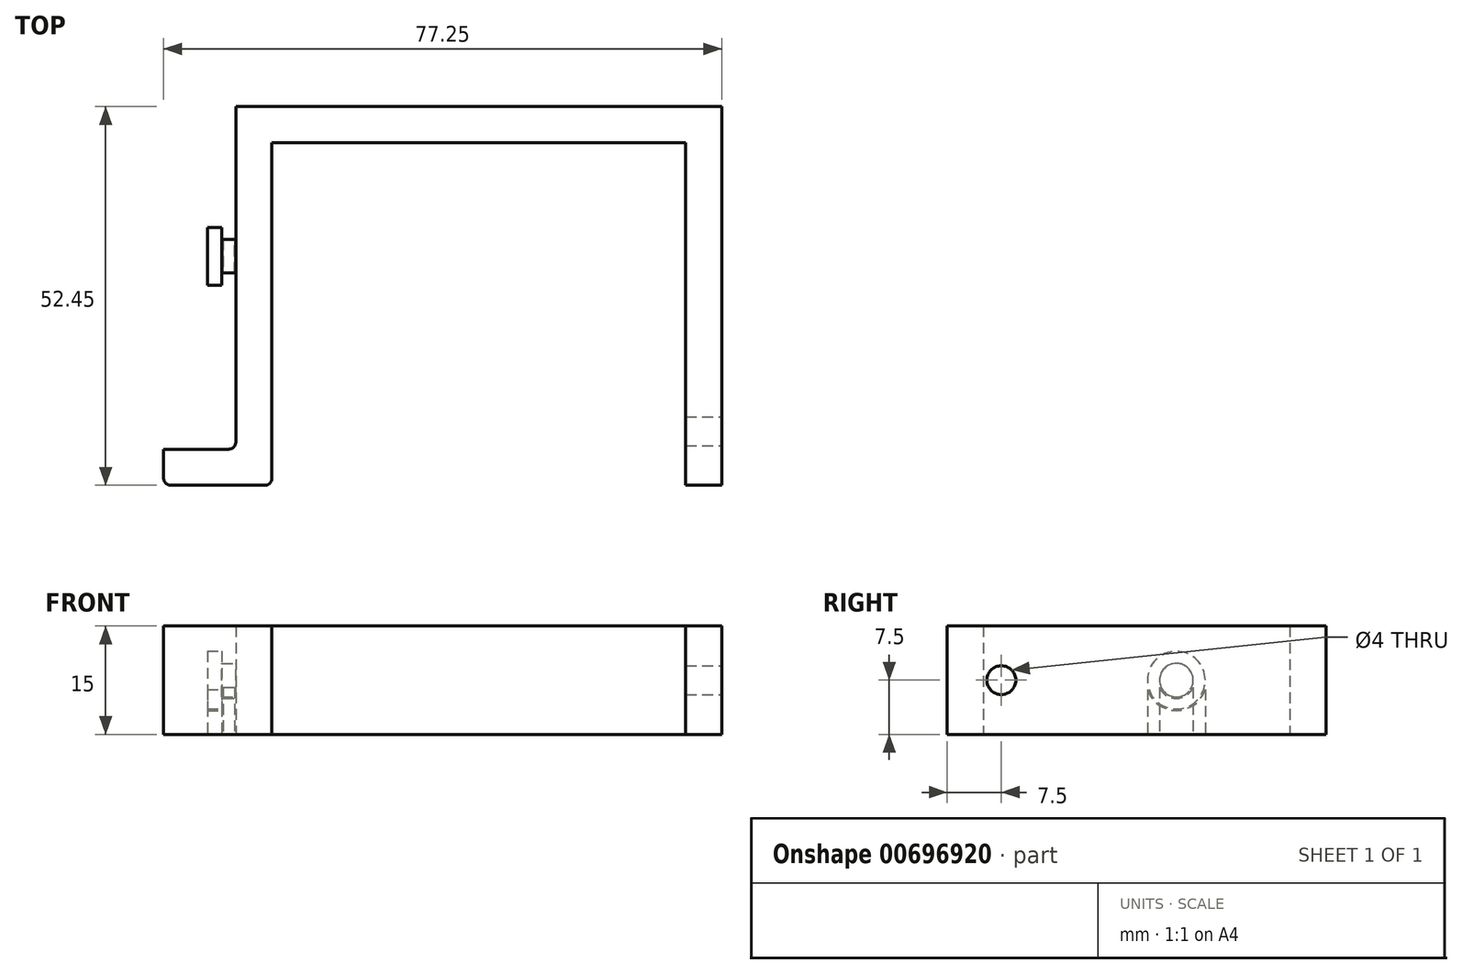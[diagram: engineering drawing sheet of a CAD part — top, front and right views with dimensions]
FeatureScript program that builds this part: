
annotation { "Feature Type Name" : "Feature", "Feature Type Description" : "" }
export const myFeature = defineFeature(function(context is Context, id is Id, definition is map)
    precondition{}
    {
        {
            var Q0;
            Q0=qCreatedBy(makeId("Top.planeOp"),FACE);
            var sketch = newSketch(context, id + "F0", { "sketchPlane" : qUnion([Q0])});
            skLineSegment(sketch, "E0.top", {"start": v(0, 20.15) * mm, "end": v(57.25, 20.15) * mm});
            skLineSegment(sketch, "E0.left", {"start": v(0, 0) * mm, "end": v(0, 20.15) * mm});
            skLineSegment(sketch, "E1.top", {"start": v(-5, 25.15) * mm, "end": v(62.25, 25.15) * mm});
            skLineSegment(sketch, "E2", {"start": v(-5, 25.15) * mm, "end": v(-5, 0) * mm});
            skLineSegment(sketch, "E3", {"start": v(0, 0) * mm, "end": v(0, -22.3) * mm});
            skLineSegment(sketch, "E4", {"start": v(-5, 0) * mm, "end": v(-5, -22.3) * mm});
            skLineSegment(sketch, "E5.bottom", {"start": v(-5, -22.3) * mm, "end": v(-15, -22.3) * mm});
            skLineSegment(sketch, "E5.top", {"start": v(0, -27.3) * mm, "end": v(-15, -27.3) * mm});
            skLineSegment(sketch, "E5.left", {"start": v(0, -22.3) * mm, "end": v(0, -27.3) * mm});
            skLineSegment(sketch, "E5.right", {"start": v(-15, -22.3) * mm, "end": v(-15, -27.3) * mm});
            skLineSegment(sketch, "E6", {"start": v(62.25, 25.15) * mm, "end": v(62.25, -27.3) * mm});
            skLineSegment(sketch, "E7", {"start": v(57.25, 20.15) * mm, "end": v(57.25, -27.3) * mm});
            skLineSegment(sketch, "E8", {"start": v(57.25, -27.3) * mm, "end": v(62.25, -27.3) * mm});
            skSolve(sketch);
        }
        {
            var Q0;
            Q0 = qSketchRegion(id + "F0", true);
            extrude(context, id + "F1", {"entities" : qUnion([Q0]), "depth" : 15 * mm, "offsetDistance" : 25 * mm});
        }
        {
            var Q0;
            Q0=makeQuery(id+"F1.opExtrude","SWEPT_FACE",FACE,{"disambiguationData":[OSD([sQuery(id+"F0.wireOp",EDGE,"E2")])]});
            var sketch = newSketch(context, id + "F2", { "sketchPlane" : qUnion([Q0])});
            skCircle(sketch, "E9", {"center": v(-4.42, 7.5) * mm, "radius": 2.33 * mm});
            skArc(sketch, "E10", {"start": v(-6.75, 6.52) * mm, "mid": v(-4.42, 4.97) * mm, "end": v(-2.1, 6.52) * mm});
            skLineSegment(sketch, "E11", {"start": v(-6.75, 6.52) * mm, "end": v(-6.75, 0) * mm});
            skLineSegment(sketch, "E12", {"start": v(-2.1, 6.52) * mm, "end": v(-2.1, 0) * mm});
            skLineSegment(sketch, "E13", {"start": v(-2.1, 0) * mm, "end": v(-6.75, 0) * mm});
            skPoint(sketch, "E14.orphan", {"position": v(-6.75, 7.5) * mm});
            skPoint(sketch, "E15.orphan", {"position": v(-2.1, 7.5) * mm});
            skSolve(sketch);
        }
        {
            var Q0;
            Q0 = qSketchRegion(id + "F2", true);
            extrude(context, id + "F3", {"entities" : qUnion([Q0]), "operationType" : NewBodyOperationType.ADD, "depth" : 1.95 * mm, "offsetDistance" : 25 * mm});
        }
        {
            var Q0;
            Q0=makeQuery(id+"F3.opExtrude","CAP_FACE",FACE,{"disambiguationData":[OSD([sQuery(id+"F2.wireOp",EDGE,"E9")])],"isStart":false});
            var sketch = newSketch(context, id + "F4", { "sketchPlane" : qUnion([Q0])});
            skCircle(sketch, "E16", {"center": v(-4.42, 7.5) * mm, "radius": 4 * mm});
            skLineSegment(sketch, "E17", {"start": v(-8.42, 6.22) * mm, "end": v(-8.42, 0) * mm});
            skLineSegment(sketch, "E18", {"start": v(-0.42, 6.22) * mm, "end": v(-0.42, 0) * mm});
            skLineSegment(sketch, "E19", {"start": v(-0.42, 0) * mm, "end": v(-8.42, 0) * mm});
            skArc(sketch, "E20", {"start": v(-8.42, 6.22) * mm, "mid": v(-4.42, 3.3) * mm, "end": v(-0.42, 6.22) * mm});
            skPoint(sketch, "E21.orphan", {"position": v(-8.42, 7.5) * mm});
            skPoint(sketch, "E22.orphan", {"position": v(-0.42, 7.5) * mm});
            skSolve(sketch);
        }
        {
            var Q0;
            Q0 = qSketchRegion(id + "F4", true);
            extrude(context, id + "F5", {"entities" : qUnion([Q0]), "operationType" : NewBodyOperationType.ADD, "depth" : 2 * mm, "offsetDistance" : 25 * mm});
        }
        {
            var Q0;
            Q0=makeQuery(id+"F5.boolean.opBoolean","MERGE",FACE,{"derivedFrom":[makeQuery(id+"F3.boolean.opBoolean","MERGE",FACE,{"derivedFrom":[makeQuery(id+"F1.opExtrude","CAP_FACE",FACE,{"disambiguationData":[OSD([sQuery(id+"F0.wireOp",EDGE,"E0.top"),sQuery(id+"F0.wireOp",EDGE,"E0.left"),sQuery(id+"F0.wireOp",EDGE,"E0.right"),sQuery(id+"F0.wireOp",EDGE,"E1.top"),sQuery(id+"F0.wireOp",EDGE,"E1.right"),sQuery(id+"F0.wireOp",EDGE,"962DIITk-y9DG-CVLt-9h3L-DnA35yfKHCaI"),sQuery(id+"F0.wireOp",EDGE,"IBw1vZgg-cOK9-ItiV-ksws-nT7VTr6wvGIP"),sQuery(id+"F0.wireOp",EDGE,"E2"),sQuery(id+"F0.wireOp",EDGE,"gIwaJglO-ZnYY-fk6S-nZtS-CVbH9vVCVLog")])],"isStart":true}),makeQuery(id+"F3.opExtrude","SWEPT_FACE",FACE,{"disambiguationData":[OSD([sQuery(id+"F2.wireOp",EDGE,"E13")])]})]}),makeQuery(id+"F5.opExtrude","SWEPT_FACE",FACE,{"disambiguationData":[OSD([sQuery(id+"F4.wireOp",EDGE,"E19")])]})]});
            var sketch = newSketch(context, id + "F6", { "sketchPlane" : qUnion([Q0])});
            skLineSegment(sketch, "E23.bottom", {"start": v(-5, -2.1) * mm, "end": v(-5.2, -2.1) * mm});
            skLineSegment(sketch, "E23.top", {"start": v(-5, -6.75) * mm, "end": v(-5.2, -6.75) * mm});
            skLineSegment(sketch, "E23.left", {"start": v(-5, -2.1) * mm, "end": v(-5, -6.75) * mm});
            skLineSegment(sketch, "E23.right", {"start": v(-5.2, -2.1) * mm, "end": v(-5.2, -6.75) * mm});
            skLineSegment(sketch, "E24.bottom", {"start": v(-6.95, -2.1) * mm, "end": v(-6.75, -2.1) * mm});
            skLineSegment(sketch, "E24.top", {"start": v(-6.95, -6.75) * mm, "end": v(-6.75, -6.75) * mm});
            skLineSegment(sketch, "E24.left", {"start": v(-6.95, -2.1) * mm, "end": v(-6.95, -6.75) * mm});
            skLineSegment(sketch, "E24.right", {"start": v(-6.75, -2.1) * mm, "end": v(-6.75, -6.75) * mm});
            skSolve(sketch);
        }
        {
            var Q0;
            Q0 = qSketchRegion(id + "F6", true);
            var Q1;
            Q1=makeQuery(id+"F3.opExtrude","SWEPT_FACE",FACE,{"disambiguationData":[OSD([sQuery(id+"F2.wireOp",EDGE,"E10")])]});
            extrude(context, id + "F7", {"entities" : qUnion([Q0]), "operationType" : NewBodyOperationType.REMOVE, "endBound" : BoundingType.UP_TO_SURFACE, "oppositeDirection" : true, "depth" : 25 * mm, "endBoundEntityFace" : qUnion([Q1]), "offsetDistance" : 25 * mm});
        }
        {
            var Q0;
            Q0=makeQuery(id+"F1.opExtrude","SWEPT_EDGE",EDGE,{"disambiguationData":[OSD([sQuery(id+"F0.wireOp",EDGE,"E4"),sQuery(id+"F0.wireOp",EDGE,"E5.bottom")])]});
            var Q1;
            Q1=makeQuery(id+"F1.opExtrude","SWEPT_EDGE",EDGE,{"disambiguationData":[OSD([sQuery(id+"F0.wireOp",EDGE,"E5.top"),sQuery(id+"F0.wireOp",EDGE,"E5.left")])]});
            var Q2;
            Q2=makeQuery(id+"F1.opExtrude","SWEPT_EDGE",EDGE,{"disambiguationData":[OSD([sQuery(id+"F0.wireOp",EDGE,"E5.top"),sQuery(id+"F0.wireOp",EDGE,"E5.right")])]});
            fillet(context, id + "F8", {"entities" : qUnion([Q0, Q1, Q2]), "radius" : 1 * mm, "tangentPropagation" : true, "allowEdgeOverflow" : false});
        }
        {
            var Q0;
            Q0=makeQuery(id+"F1.opExtrude","SWEPT_FACE",FACE,{"disambiguationData":[OSD([sQuery(id+"F0.wireOp",EDGE,"E6")])]});
            var sketch = newSketch(context, id + "F9", { "sketchPlane" : qUnion([Q0])});
            skCircle(sketch, "E25", {"center": v(-19.8, 7.5) * mm, "radius": 2 * mm});
            skSolve(sketch);
        }
        {
            var Q0;
            Q0 = qSketchRegion(id + "F9", true);
            extrude(context, id + "F10", {"entities" : qUnion([Q0]), "operationType" : NewBodyOperationType.REMOVE, "endBound" : BoundingType.UP_TO_NEXT, "oppositeDirection" : true, "depth" : 25 * mm, "offsetDistance" : 25 * mm});
        }
    });
